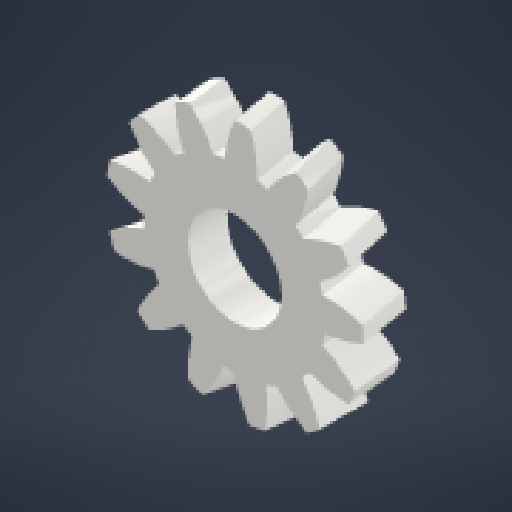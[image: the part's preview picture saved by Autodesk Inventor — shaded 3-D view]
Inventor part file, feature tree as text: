
AUTODESK INVENTOR PART (.ipt)
format: ipt  version: 2024.2 (Build 282272000, 272)  size: 358,400 bytes
history: native  units: mm (DEFAULTED — no unit token found)
features: extrude x3, plane x3, other x3, sketch x3
ambient origin geometry x8: Origin, YZ Plane, XZ Plane, XY Plane, X Axis, Y Axis, Z Axis, Center Point
bodies: Solid1 (feature_tree)
feature tree (12):
  extrude  "Extrusion1"  Depth=6.35mm TaperAngle=0.0deg
  plane  "Work Plane1"
  plane  "Work Plane2"
  plane  "Work Plane3"
  other  "Spur Gear"
  extrude  "Extrusion2"  Depth=76.2mm TaperAngle=0.0deg
  extrude  "Extrusion3"  TaperAngle=0.0deg  [1 undecoded]
  sketch  "Sketch1"  dims[d0=38.570605mm d1=6.35mm d2=0.0mm]
  other  "Srf1"
  sketch  "Sketch3"  dims[d3=33.529387mm d4=76.2mm d5=0.0mm]
  sketch  "Sketch4"  dims[d6=0.0mm d7=2.41661mm d9=0.0mm d14=0.0mm d15=35.513307mm d16=0.0mm d17=0.0mm d18=0.0mm d19=35.513307mm d20=15.0mm d21=1.0mm d22=0.0mm d23=14.0mm d24=0.0mm d25=0.0mm]
  other  "Pitch Diameter"
note: 1 required parameter value undecoded (feature->parameter linkage not recoverable at this tier; creation-order binding heuristic only, values carry confidence <= 0.55)
